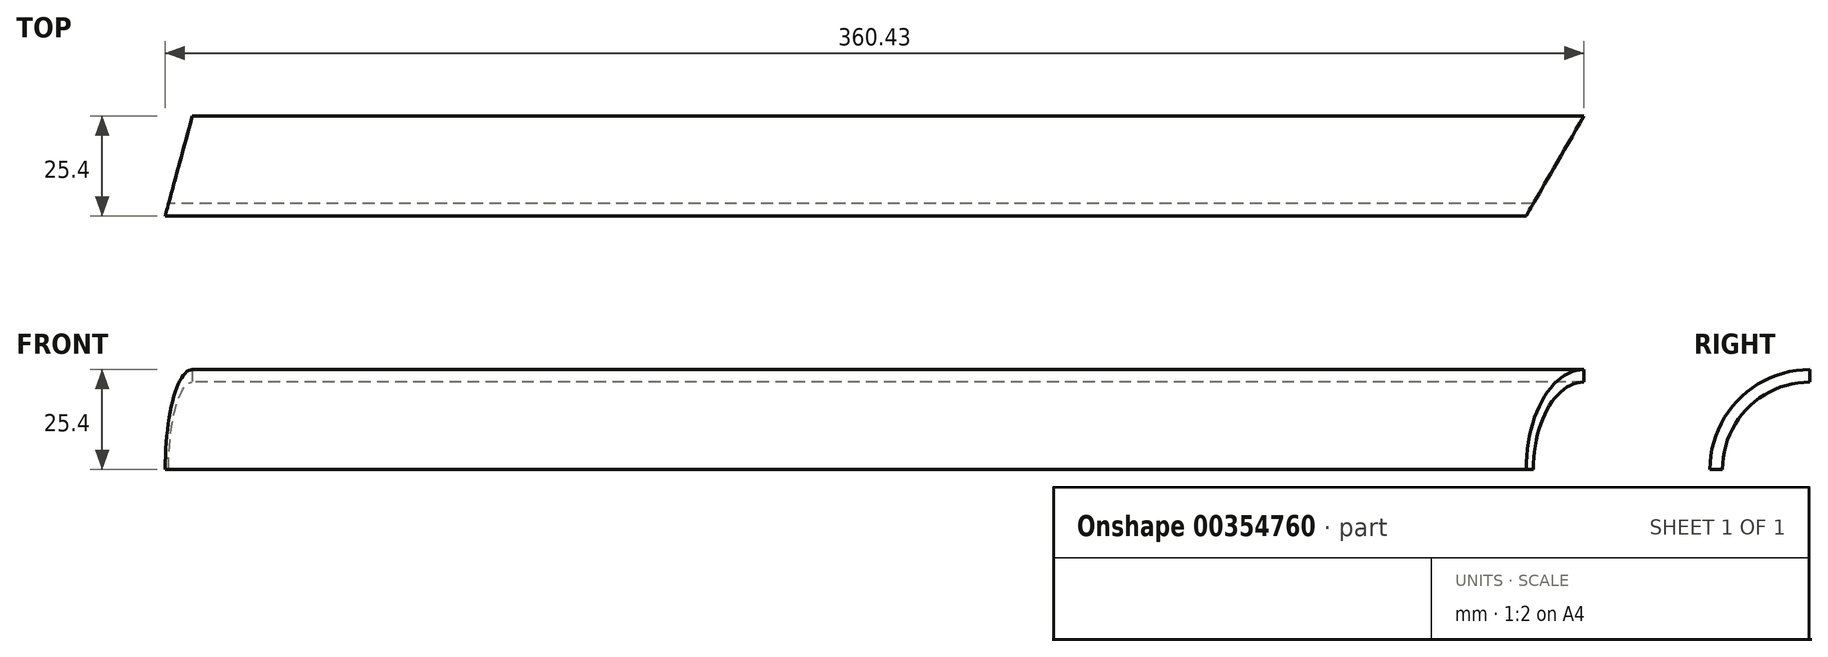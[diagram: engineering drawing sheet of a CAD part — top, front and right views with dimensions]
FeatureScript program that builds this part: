
annotation { "Feature Type Name" : "Feature", "Feature Type Description" : "" }
export const myFeature = defineFeature(function(context is Context, id is Id, definition is map)
    precondition{}
    {
        {
            var Q0;
            Q0=qCreatedBy(makeId("Right.planeOp"),FACE);
            var sketch = newSketch(context, id + "F0", { "sketchPlane" : qUnion([Q0])});
            skArc(sketch, "E0", {"start": v(-25.4, 0) * mm, "mid": v(-17.96, 17.96) * mm, "end": v(0, 25.4) * mm});
            skArc(sketch, "E1.0", {"start": v(-22.23, 0) * mm, "mid": v(-15.72, 15.72) * mm, "end": v(0, 22.23) * mm});
            skLineSegment(sketch, "E2", {"start": v(-25.4, 0) * mm, "end": v(-22.23, 0) * mm});
            skLineSegment(sketch, "E3", {"start": v(0, 25.4) * mm, "end": v(0, 22.23) * mm});
            skSolve(sketch);
        }
        {
            var Q0;
            Q0 = qSketchRegion(id + "F0", true);
            extrude(context, id + "F1", {"entities" : qUnion([Q0]), "depth" : 360.43 * mm});
        }
        {
            var Q0;
            Q0=qCreatedBy(makeId("Top.planeOp"),FACE);
            var sketch = newSketch(context, id + "F2", { "sketchPlane" : qUnion([Q0])});
            skLineSegment(sketch, "E4", {"start": v(0, 0) * mm, "end": v(0, -25.4) * mm});
            skLineSegment(sketch, "E5", {"start": v(0, -25.4) * mm, "end": v(6.9, 0) * mm});
            skLineSegment(sketch, "E6", {"start": v(6.9, 0) * mm, "end": v(0, 0) * mm});
            skLineSegment(sketch, "E7", {"start": v(360.43, 0) * mm, "end": v(345.76, -25.4) * mm});
            skLineSegment(sketch, "E8", {"start": v(345.76, -25.4) * mm, "end": v(360.43, -25.4) * mm});
            skLineSegment(sketch, "E9", {"start": v(360.43, -25.4) * mm, "end": v(360.43, 0) * mm});
            skSolve(sketch);
        }
        {
            var Q0;
            Q0 = qSketchRegion(id + "F2", true);
            extrude(context, id + "F3", {"entities" : qUnion([Q0]), "operationType" : NewBodyOperationType.REMOVE, "depth" : 25.4 * mm});
        }
    });
